# Revit family: P210876JX-004_JUBFL242HX_JUBFR242HX
name_source: partatom
category: Specialty Equipment
units: mm (PartAtom-declared; Revit-internal decimal feet)

## family parameters
Always vertical = Yes
Cut with Voids When Loaded = No
Enable Cutting in Views = No
Maintain Annotation Orientation = No
Part Type = Normal
Room Calculation Point = No
Round Connector Dimension = Use Diameter
Shared = No
Work Plane-Based = No

## types (1)
- JUBFL242HX
    Amps = 0 A
    Back Panel Material = ARCAT - Metal - Aluminum
    Body Material = ARCAT - Metal - Steel - Black
    Bottom Panel Material = ARCAT - Metal - Steel - Black
    Clearance Material = ARCAT - Clearance
    Default Elevation = 0"
    Depth = 23 11/16"
    Description = Panel-Ready 24" Built-In Undercounter Beverage Center, Left Swing
Centre de rafraîchissements, panneau, charnière à gauche, 24 po
    Dimension Guide = https://whirlpool.com
https://whirlpool.com
    Door Material = ARCAT - Metal - Steel - Black - Light
    Energy Guide = https://www.whirlpool.com
https://www.whirlpool.com
    Family Name = Beverage Center Specialty
    Feature 1 = Daring Obsidian Interior
Daring Obsidian Interior
    Feature 2 = Emotive Controls
Emotive Controls
    Feature 3 = Glass Shelves
Tablettes en verre
    Glass Material = ARCAT - Glass - Gray
    Handle Material = ARCAT - Metal - Brass
    Height = 34 1/8"
    Hinge Material = ARCAT - Plastic - Black
    Leg Material = ARCAT - Plastic - Black
    Manufacturer = JennAir
    Model = JUBFL242HX
    Screw Material = ARCAT - Metal - Steel - Stainless
    Tray Material = ARCAT - Metal - Steel - Stainless
    Voltage = 0 V
    Width = 23 7/8"

## geometry (parser evidence)
native form markers: Sweep x2
no freeform markers — native parametric forms only
